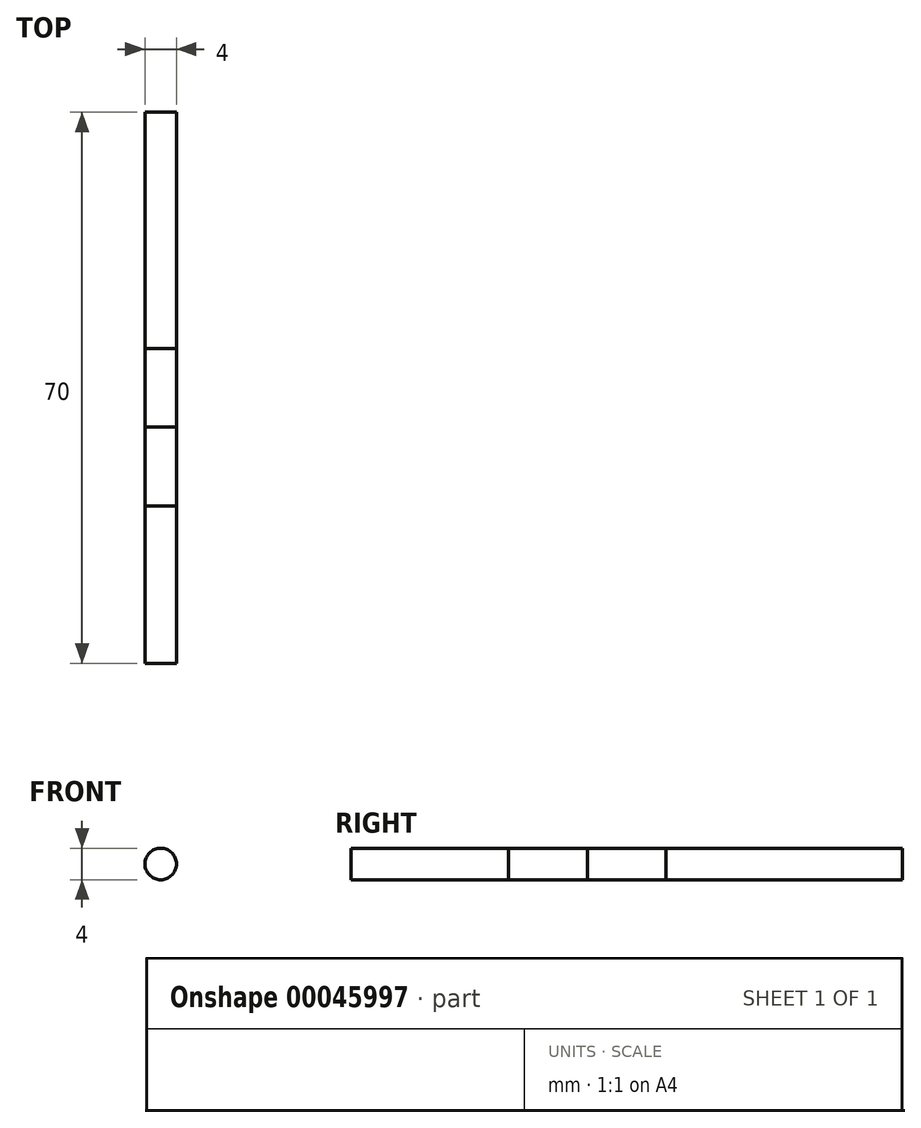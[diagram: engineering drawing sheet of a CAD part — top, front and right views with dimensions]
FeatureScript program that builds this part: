
annotation { "Feature Type Name" : "Feature", "Feature Type Description" : "" }
export const myFeature = defineFeature(function(context is Context, id is Id, definition is map)
    precondition{}
    {
        {
            var Q0;
            Q0=qCreatedBy(makeId("Front.planeOp"),FACE);
            var sketch = newSketch(context, id + "F0", { "sketchPlane" : qUnion([Q0])});
            skCircle(sketch, "E0", {"center": v(0, 0) * mm, "radius": 2 * mm});
            skSolve(sketch);
        }
        {
            var Q0;
            Q0 = qSketchRegion(id + "F0", true);
            extrude(context, id + "F1", {"entities" : qUnion([Q0]), "depth" : 20 * mm});
        }
        {
            var Q0;
            Q0=makeQuery(id+"F0.imprint","IMPRINT",FACE,{"disambiguationData":[TD([[makeQuery(id+"F0.imprint","IMPRINT",EDGE,{"derivedFrom":sQuery(id+"F0.wireOp",EDGE,"E0")}),1.0]])]});
            extrude(context, id + "F2", {"entities" : qUnion([Q0]), "oppositeDirection" : true, "depth" : 30 * mm});
        }
        {
            var Q0;
            Q0 = qSketchRegion(id + "F0", true);
            extrude(context, id + "F3", {"entities" : qUnion([Q0]), "depth" : 40 * mm});
        }
        {
            var Q0;
            Q0=makeQuery(id+"F0.imprint","IMPRINT",FACE,{"disambiguationData":[TD([[makeQuery(id+"F0.imprint","IMPRINT",EDGE,{"derivedFrom":sQuery(id+"F0.wireOp",EDGE,"E0")}),1.0]])]});
            extrude(context, id + "F4", {"entities" : qUnion([Q0]), "depth" : 10 * mm});
        }
    });
